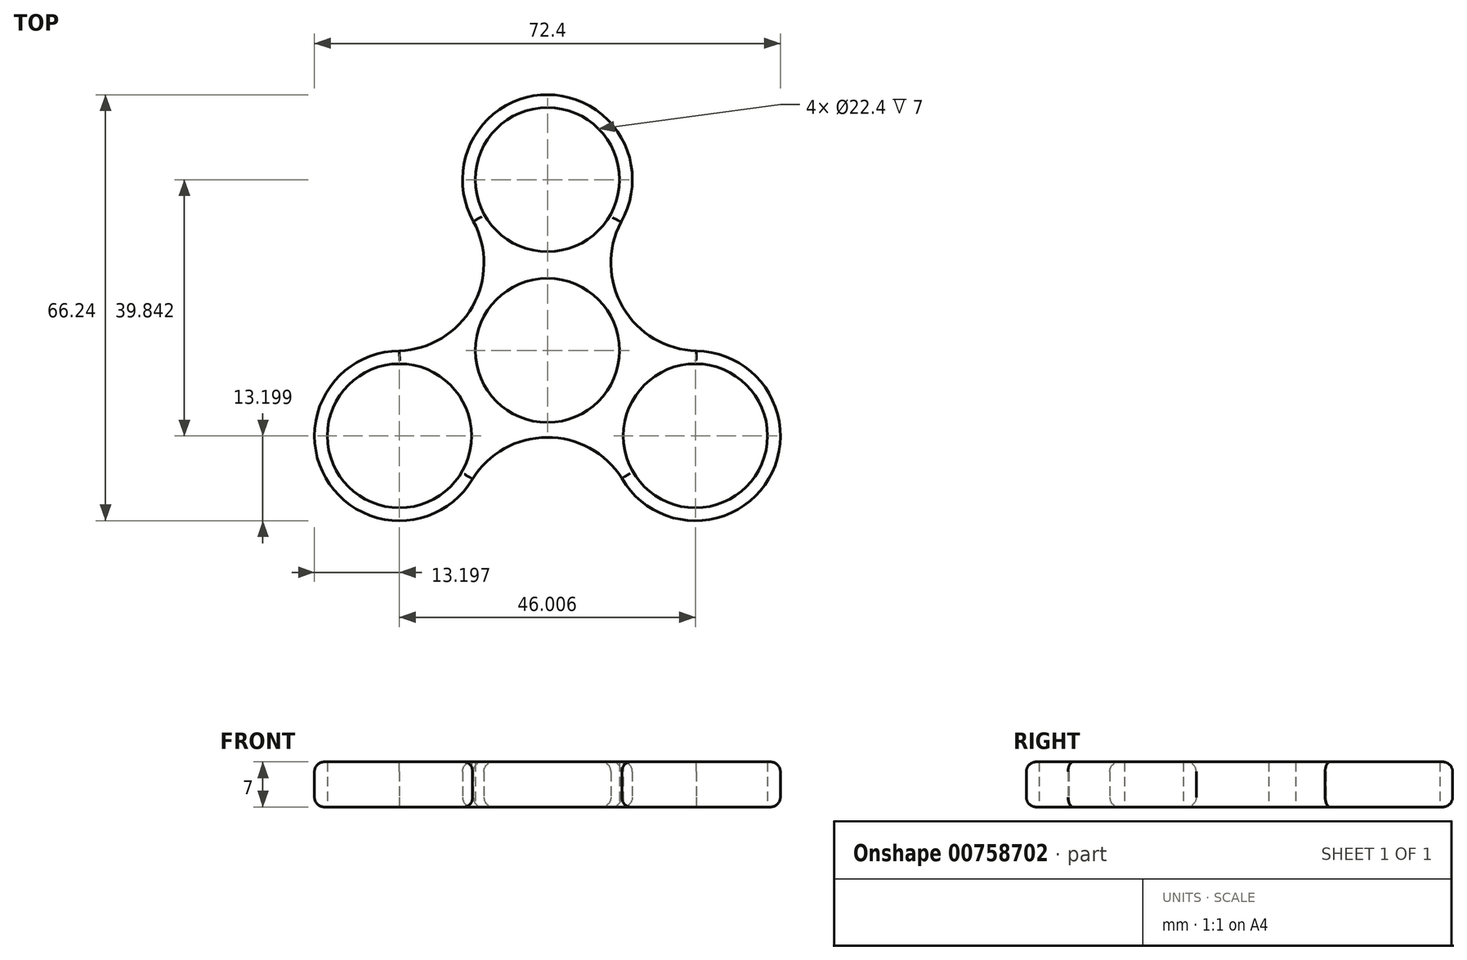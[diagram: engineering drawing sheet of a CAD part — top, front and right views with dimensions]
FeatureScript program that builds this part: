
annotation { "Feature Type Name" : "Feature", "Feature Type Description" : "" }
export const myFeature = defineFeature(function(context is Context, id is Id, definition is map)
    precondition{}
    {
        {
            var Q0;
            Q0=qCreatedBy(makeId("Top.planeOp"),FACE);
            var sketch = newSketch(context, id + "F0", { "sketchPlane" : qUnion([Q0])});
            skCircle(sketch, "E0", {"center": v(0, 0) * mm, "radius": 11.2 * mm});
            skCircle(sketch, "E1", {"center": v(0, 26.56) * mm, "radius": 11.2 * mm});
            skArc(sketch, "E2", {"start": v(11.43, 19.96) * mm, "mid": v(0.07, 39.76) * mm, "end": v(-11.5, 20.08) * mm});
            skArc(sketch, "E3.1.0", {"start": v(-23, -0.08) * mm, "mid": v(-34.47, -19.82) * mm, "end": v(-11.64, -20) * mm});
            skCircle(sketch, "E3.1.1", {"center": v(-23, -13.28) * mm, "radius": 11.2 * mm});
            skArc(sketch, "E3.2.0", {"start": v(11.57, -19.88) * mm, "mid": v(34.4, -19.94) * mm, "end": v(23.14, -0.08) * mm});
            skCircle(sketch, "E3.2.1", {"center": v(23, -13.28) * mm, "radius": 11.2 * mm});
            skArc(sketch, "E4", {"start": v(11.7, 20.44) * mm, "mid": v(11.67, 6.82) * mm, "end": v(23.41, -0.09) * mm});
            skArc(sketch, "E5.1.0", {"start": v(-23.55, -0.1) * mm, "mid": v(-11.74, 6.7) * mm, "end": v(-11.63, 20.32) * mm});
            skArc(sketch, "E5.2.0", {"start": v(11.85, -20.35) * mm, "mid": v(0.07, -13.51) * mm, "end": v(-11.78, -20.23) * mm});
            skSolve(sketch);
        }
        {
            var Q0;
            Q0 = qSketchRegion(id + "F0", true);
            extrude(context, id + "F1", {"entities" : qUnion([Q0]), "depth" : 7 * mm, "offsetDistance" : 25 * mm});
        }
        {
            var Q0;
            Q0=makeQuery(id+"F1.opExtrude","CAP_EDGE",EDGE,{"disambiguationData":[OSD([sQuery(id+"F0.wireOp",EDGE,"E5.2.0")])],"isStart":false});
            var Q1;
            Q1=makeQuery(id+"F1.opExtrude","CAP_EDGE",EDGE,{"disambiguationData":[OSD([sQuery(id+"F0.wireOp",EDGE,"E5.2.0")])],"isStart":true});
            var Q2;
            Q2=makeQuery(id+"F1.opExtrude","CAP_EDGE",EDGE,{"disambiguationData":[OSD([sQuery(id+"F0.wireOp",EDGE,"E3.1.0")])],"isStart":false});
            var Q3;
            Q3=makeQuery(id+"F1.opExtrude","CAP_EDGE",EDGE,{"disambiguationData":[OSD([sQuery(id+"F0.wireOp",EDGE,"E5.1.0")])],"isStart":false});
            var Q4;
            Q4=makeQuery(id+"F1.opExtrude","CAP_EDGE",EDGE,{"disambiguationData":[OSD([sQuery(id+"F0.wireOp",EDGE,"E2")])],"isStart":false});
            var Q5;
            Q5=makeQuery(id+"F1.opExtrude","CAP_EDGE",EDGE,{"disambiguationData":[OSD([sQuery(id+"F0.wireOp",EDGE,"E4")])],"isStart":false});
            var Q6;
            Q6=makeQuery(id+"F1.opExtrude","CAP_EDGE",EDGE,{"disambiguationData":[OSD([sQuery(id+"F0.wireOp",EDGE,"E3.2.0")])],"isStart":false});
            fillet(context, id + "F2", {"entities" : qUnion([Q0, Q1, Q2, Q3, Q4, Q5, Q6]), "radius" : 1.5 * mm, "tangentPropagation" : true, "allowEdgeOverflow" : false});
        }
        {
            var Q0;
            Q0=makeQuery(id+"F1.opExtrude","CAP_EDGE",EDGE,{"disambiguationData":[OSD([sQuery(id+"F0.wireOp",EDGE,"E3.1.0")])],"isStart":true});
            var Q1;
            Q1=makeQuery(id+"F1.opExtrude","CAP_EDGE",EDGE,{"disambiguationData":[OSD([sQuery(id+"F0.wireOp",EDGE,"E5.1.0")])],"isStart":true});
            var Q2;
            Q2=makeQuery(id+"F1.opExtrude","CAP_EDGE",EDGE,{"disambiguationData":[OSD([sQuery(id+"F0.wireOp",EDGE,"E2")])],"isStart":true});
            var Q3;
            Q3=makeQuery(id+"F1.opExtrude","CAP_EDGE",EDGE,{"disambiguationData":[OSD([sQuery(id+"F0.wireOp",EDGE,"E4")])],"isStart":true});
            var Q4;
            Q4=makeQuery(id+"F1.opExtrude","CAP_EDGE",EDGE,{"disambiguationData":[OSD([sQuery(id+"F0.wireOp",EDGE,"E3.2.0")])],"isStart":true});
            var Q5;
            {var subQ0=sQuery(id+"F0.wireOp",EDGE,"E5.2.0");Q5=makeQuery(id+"F2.opFillet","BLEND_EDGE",EDGE,{"blendedFrom":[makeQuery(id+"F1.opExtrude","CAP_EDGE",EDGE,{"disambiguationData":[OSD([subQ0])],"isStart":true}),makeQuery(id+"F1.opExtrude","CAP_FACE",FACE,{"disambiguationData":[OSD([sQuery(id+"F0.wireOp",EDGE,"E0"),sQuery(id+"F0.wireOp",EDGE,"E1"),sQuery(id+"F0.wireOp",EDGE,"E2"),sQuery(id+"F0.wireOp",EDGE,"E3.1.0"),sQuery(id+"F0.wireOp",EDGE,"E3.1.1"),sQuery(id+"F0.wireOp",EDGE,"E3.2.0"),sQuery(id+"F0.wireOp",EDGE,"E3.2.1"),sQuery(id+"F0.wireOp",EDGE,"E4"),sQuery(id+"F0.wireOp",EDGE,"E5.1.0"),subQ0])],"isStart":true})],"blendedInto":[makeQuery(id+"F1.opExtrude","CAP_FACE",FACE,{"disambiguationData":[OSD([sQuery(id+"F0.wireOp",EDGE,"E0"),sQuery(id+"F0.wireOp",EDGE,"E1"),sQuery(id+"F0.wireOp",EDGE,"E2"),sQuery(id+"F0.wireOp",EDGE,"E3.1.0"),sQuery(id+"F0.wireOp",EDGE,"E3.1.1"),sQuery(id+"F0.wireOp",EDGE,"E3.2.0"),sQuery(id+"F0.wireOp",EDGE,"E3.2.1"),sQuery(id+"F0.wireOp",EDGE,"E4"),sQuery(id+"F0.wireOp",EDGE,"E5.1.0"),subQ0])],"isStart":true})]});}
            fillet(context, id + "F3", {"entities" : qUnion([Q0, Q1, Q2, Q3, Q4, Q5]), "radius" : 1.5 * mm, "tangentPropagation" : true, "allowEdgeOverflow" : false});
        }
    });
